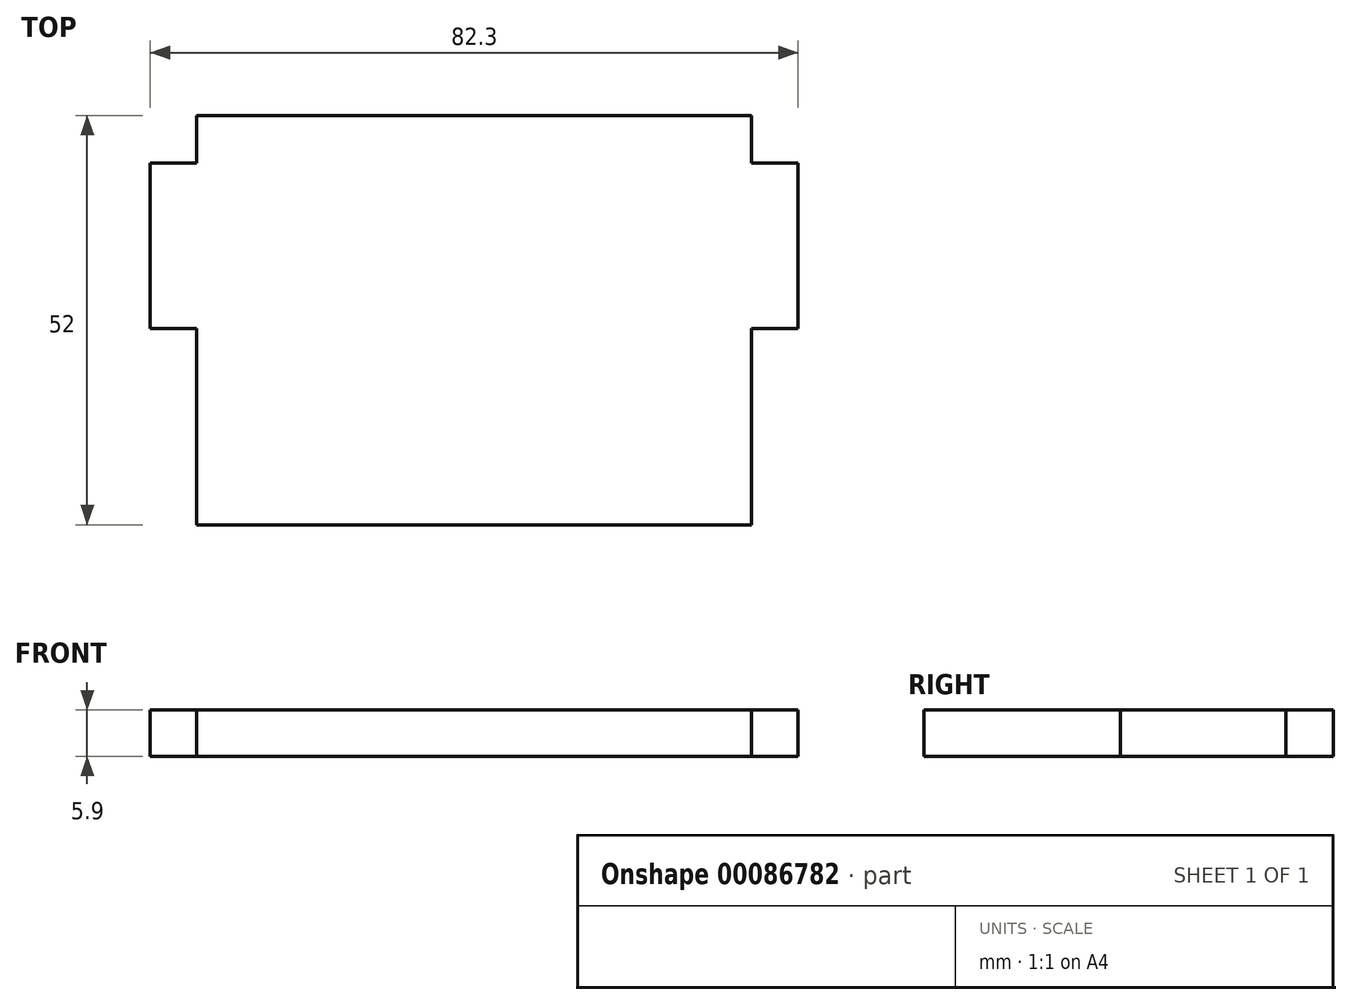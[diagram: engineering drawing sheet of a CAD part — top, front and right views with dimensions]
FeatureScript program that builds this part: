
annotation { "Feature Type Name" : "Feature", "Feature Type Description" : "" }
export const myFeature = defineFeature(function(context is Context, id is Id, definition is map)
    precondition{}
    {
        {
            var Q0;
            Q0=qCreatedBy(makeId("Top.planeOp"),FACE);
            var sketch = newSketch(context, id + "F0", { "sketchPlane" : qUnion([Q0])});
            skLineSegment(sketch, "E0.bottom", {"start": v(35.25, 26) * mm, "end": v(-35.25, 26) * mm});
            skLineSegment(sketch, "E0.top", {"start": v(35.25, -26) * mm, "end": v(-35.25, -26) * mm});
            skLineSegment(sketch, "E0.left", {"start": v(35.25, 26) * mm, "end": v(35.25, -26) * mm});
            skLineSegment(sketch, "E0.right", {"start": v(-35.25, 26) * mm, "end": v(-35.25, -26) * mm});
            skPoint(sketch, "E0.middle", {"position": v(0, 0) * mm});
            skLineSegment(sketch, "E1.bottom", {"start": v(-35.25, -1.05) * mm, "end": v(-41.15, -1.05) * mm});
            skLineSegment(sketch, "E1.top", {"start": v(-35.25, 19.95) * mm, "end": v(-41.15, 19.95) * mm});
            skLineSegment(sketch, "E1.left", {"start": v(-35.25, -1.05) * mm, "end": v(-35.25, 19.95) * mm});
            skLineSegment(sketch, "E1.right", {"start": v(-41.15, -1.05) * mm, "end": v(-41.15, 19.95) * mm});
            skLineSegment(sketch, "E2.MirrorCS", {"start": v(35.25, 19.95) * mm, "end": v(41.15, 19.95) * mm});
            skLineSegment(sketch, "E3.MirrorCS", {"start": v(41.15, -1.05) * mm, "end": v(41.15, 19.95) * mm});
            skLineSegment(sketch, "E4.MirrorCS", {"start": v(35.25, -1.05) * mm, "end": v(41.15, -1.05) * mm});
            skSolve(sketch);
        }
        {
            var Q0;
            Q0 = qSketchRegion(id + "F0", true);
            extrude(context, id + "F1", {"entities" : qUnion([Q0]), "depth" : 5.9 * mm});
        }
    });
